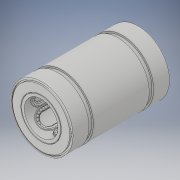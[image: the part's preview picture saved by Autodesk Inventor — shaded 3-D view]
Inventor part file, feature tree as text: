
AUTODESK INVENTOR PART (.ipt)
format: ipt  version: 2017 (Build 210142000, 142)  size: 2,786,816 bytes
history: native  units: in
note: dims shown in document units (in); Inventor stores cm internally (conversion verified against a paired STEP export)
features: extrude x4, sketch x2, other x1, boolean_combine x1
ambient origin geometry x8: Origin, YZ Plane, XZ Plane, XY Plane, X Axis, Y Axis, Z Axis, Center Point
bodies: Solid1 (feature_tree), Solid2 (feature_tree), Solid3 (feature_tree)
feature tree (8):
  other  "61205K750_FIXED ALIGNMENT LINEAR BALL BRNG.STEP"
  extrude  "Extrusion1"  TaperAngle=0.0deg  [1 undecoded]
  extrude  "Extrusion2"  [1 undecoded]
  sketch  "Sketch1"  dims[d0=0.0in d1=0.0in d2=0.0in d3=0.0in]
  sketch  "Sketch2"
  extrude  "Extrude5"  [1 undecoded]
  extrude  "Extrude6"  [1 undecoded]
  boolean_combine  "Combine1"
note: 4 required parameter values undecoded (feature->parameter linkage not recoverable at this tier; creation-order binding heuristic only, values carry confidence <= 0.55)
